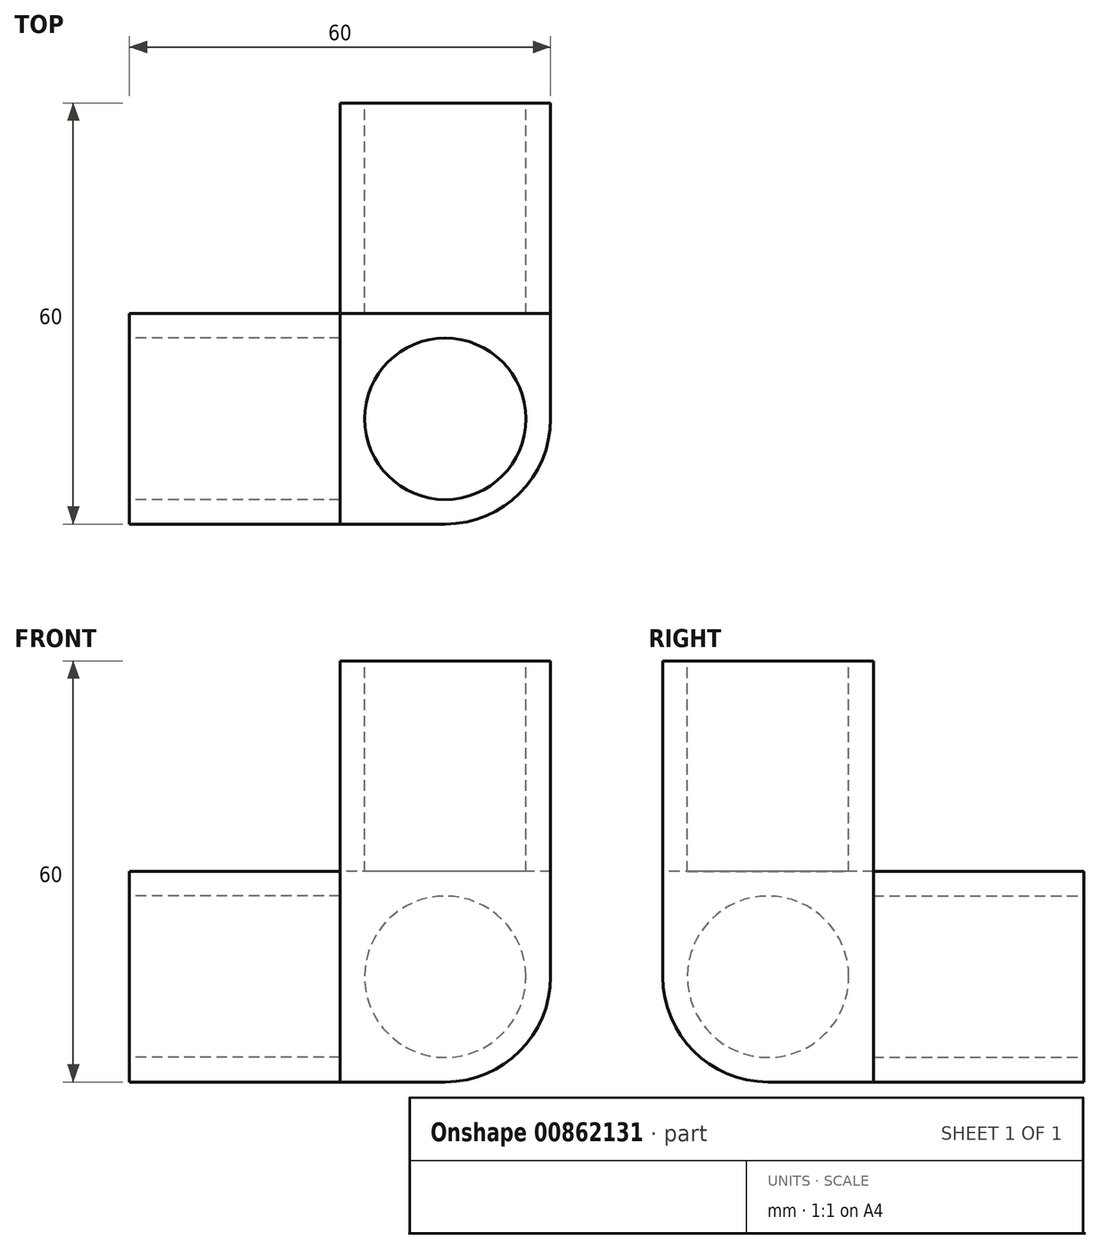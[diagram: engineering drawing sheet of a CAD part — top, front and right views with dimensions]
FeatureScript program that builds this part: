
annotation { "Feature Type Name" : "Feature", "Feature Type Description" : "" }
export const myFeature = defineFeature(function(context is Context, id is Id, definition is map)
    precondition{}
    {
        {
            var Q0;
            Q0=qCreatedBy(makeId("Top.planeOp"),FACE);
            var sketch = newSketch(context, id + "F0", { "sketchPlane" : qUnion([Q0])});
            skLineSegment(sketch, "E0", {"start": v(0, 0) * mm, "end": v(0, 30) * mm});
            skLineSegment(sketch, "E1", {"start": v(0, 30) * mm, "end": v(30, 30) * mm});
            skLineSegment(sketch, "E2", {"start": v(30, 30) * mm, "end": v(30, -30) * mm});
            skLineSegment(sketch, "E3", {"start": v(30, -30) * mm, "end": v(-30, -30) * mm});
            skLineSegment(sketch, "E4", {"start": v(-30, -30) * mm, "end": v(-30, 0) * mm});
            skLineSegment(sketch, "E5", {"start": v(-30, 0) * mm, "end": v(0, 0) * mm});
            skLineSegment(sketch, "E6", {"start": v(0, 0) * mm, "end": v(0, -30) * mm});
            skLineSegment(sketch, "E7", {"start": v(30, 0) * mm, "end": v(0, 0) * mm});
            skSolve(sketch);
        }
        {
            var Q0;
            {var subQ0=sQuery(id+"F0.wireOp",EDGE,"E4");Q0=makeQuery(id+"F0.imprint","IMPRINT",FACE,{"disambiguationData":[TD([[makeQuery(id+"F0.imprint","IMPRINT",EDGE,{"derivedFrom":subQ0}),-1.0]])]});}
            var Q1;
            Q1=makeQuery(id+"F0.imprint","IMPRINT",FACE,{"disambiguationData":[TD([[makeQuery(id+"F0.imprint","IMPRINT",EDGE,{"derivedFrom":sQuery(id+"F0.wireOp",EDGE,"E0")}),-1.0]])]});
            extrude(context, id + "F1", {"entities" : qUnion([Q0, Q1]), "depth" : 30 * mm, "offsetDistance" : 25 * mm});
        }
        {
            var Q0;
            {var subQ4=sQuery(id+"F0.wireOp",EDGE,"E6");Q0=makeQuery(id+"F0.imprint","IMPRINT",FACE,{"disambiguationData":[TD([[makeQuery(id+"F0.imprint","IMPRINT",EDGE,{"derivedFrom":subQ4}),1.0]])]});}
            extrude(context, id + "F2", {"entities" : qUnion([Q0]), "depth" : 60 * mm, "offsetDistance" : 25 * mm});
        }
        {
            var Q0;
            Q0=makeQuery(id+"F2.opExtrude","CAP_FACE",FACE,{"disambiguationData":[OSD([sQuery(id+"F0.wireOp",EDGE,"E2"),sQuery(id+"F0.wireOp",EDGE,"E3"),sQuery(id+"F0.wireOp",EDGE,"E6"),sQuery(id+"F0.wireOp",EDGE,"E7")])],"isStart":false});
            var sketch = newSketch(context, id + "F3", { "sketchPlane" : qUnion([Q0])});
            skCircle(sketch, "E8", {"center": v(15, -15) * mm, "radius": 11.5 * mm});
            skPoint(sketch, "E8.centerSnap0", {"position": v(0, -15) * mm});
            skPoint(sketch, "E8.centerSnap1", {"position": v(15, 0) * mm});
            skSolve(sketch);
        }
        {
            var Q0;
            Q0=makeQuery(id+"F1.opExtrude","SWEPT_FACE",FACE,{"disambiguationData":[OSD([sQuery(id+"F0.wireOp",EDGE,"E1")])]});
            var sketch = newSketch(context, id + "F4", { "sketchPlane" : qUnion([Q0])});
            skCircle(sketch, "E9", {"center": v(-15, 15) * mm, "radius": 11.5 * mm});
            skPoint(sketch, "E9.centerSnap0", {"position": v(0, 15) * mm});
            skPoint(sketch, "E9.centerSnap1", {"position": v(-15, 30) * mm});
            skSolve(sketch);
        }
        {
            var Q0;
            Q0=makeQuery(id+"F1.opExtrude","SWEPT_FACE",FACE,{"disambiguationData":[OSD([sQuery(id+"F0.wireOp",EDGE,"E4")])]});
            var sketch = newSketch(context, id + "F5", { "sketchPlane" : qUnion([Q0])});
            skCircle(sketch, "E10", {"center": v(15, 15) * mm, "radius": 11.5 * mm});
            skPoint(sketch, "E10.centerSnap0", {"position": v(0, 15) * mm});
            skPoint(sketch, "E10.centerSnap1", {"position": v(15, 30) * mm});
            skSolve(sketch);
        }
        {
            var Q0;
            Q0=makeQuery(id+"F4.imprint","IMPRINT",FACE,{"disambiguationData":[TD([[makeQuery(id+"F4.imprint","IMPRINT",EDGE,{"derivedFrom":sQuery(id+"F4.wireOp",EDGE,"E9")}),1.0]])]});
            extrude(context, id + "F6", {"entities" : qUnion([Q0]), "operationType" : NewBodyOperationType.REMOVE, "oppositeDirection" : true, "depth" : 30 * mm, "offsetDistance" : 25 * mm});
        }
        {
            var Q0;
            Q0=makeQuery(id+"F5.imprint","IMPRINT",FACE,{"disambiguationData":[TD([[makeQuery(id+"F5.imprint","IMPRINT",EDGE,{"derivedFrom":sQuery(id+"F5.wireOp",EDGE,"E10")}),1.0]])]});
            extrude(context, id + "F7", {"entities" : qUnion([Q0]), "operationType" : NewBodyOperationType.REMOVE, "oppositeDirection" : true, "depth" : 30 * mm, "offsetDistance" : 25 * mm});
        }
        {
            var Q0;
            Q0=makeQuery(id+"F3.imprint","IMPRINT",FACE,{"disambiguationData":[TD([[makeQuery(id+"F3.imprint","IMPRINT",EDGE,{"derivedFrom":sQuery(id+"F3.wireOp",EDGE,"E8")}),1.0]])]});
            extrude(context, id + "F8", {"entities" : qUnion([Q0]), "operationType" : NewBodyOperationType.REMOVE, "oppositeDirection" : true, "depth" : 30 * mm, "offsetDistance" : 25 * mm});
        }
        {
            var Q0;
            Q0=makeQuery(id+"F2.opExtrude","CAP_EDGE",EDGE,{"disambiguationData":[OSD([sQuery(id+"F0.wireOp",EDGE,"E3")])],"isStart":true});
            var Q1;
            Q1=makeQuery(id+"F2.opExtrude","CAP_EDGE",EDGE,{"disambiguationData":[OSD([sQuery(id+"F0.wireOp",EDGE,"E2")])],"isStart":true});
            var Q2;
            Q2=makeQuery(id+"F2.opExtrude","SWEPT_EDGE",EDGE,{"disambiguationData":[OSD([sQuery(id+"F0.wireOp",EDGE,"E2"),sQuery(id+"F0.wireOp",EDGE,"E3")])]});
            var Q3;
            Q3=makeQuery(id+"F1.opExtrude","CAP_EDGE",EDGE,{"disambiguationData":[OSD([sQuery(id+"F0.wireOp",EDGE,"E3")])],"isStart":true});
            var Q4;
            Q4=makeQuery(id+"F1.opExtrude","CAP_EDGE",EDGE,{"disambiguationData":[OSD([sQuery(id+"F0.wireOp",EDGE,"E2")])],"isStart":true});
            fillet(context, id + "F9", {"entities" : qUnion([Q0, Q1, Q2, Q3, Q4]), "radius" : 15 * mm, "tangentPropagation" : true, "allowEdgeOverflow" : false});
        }
    });
